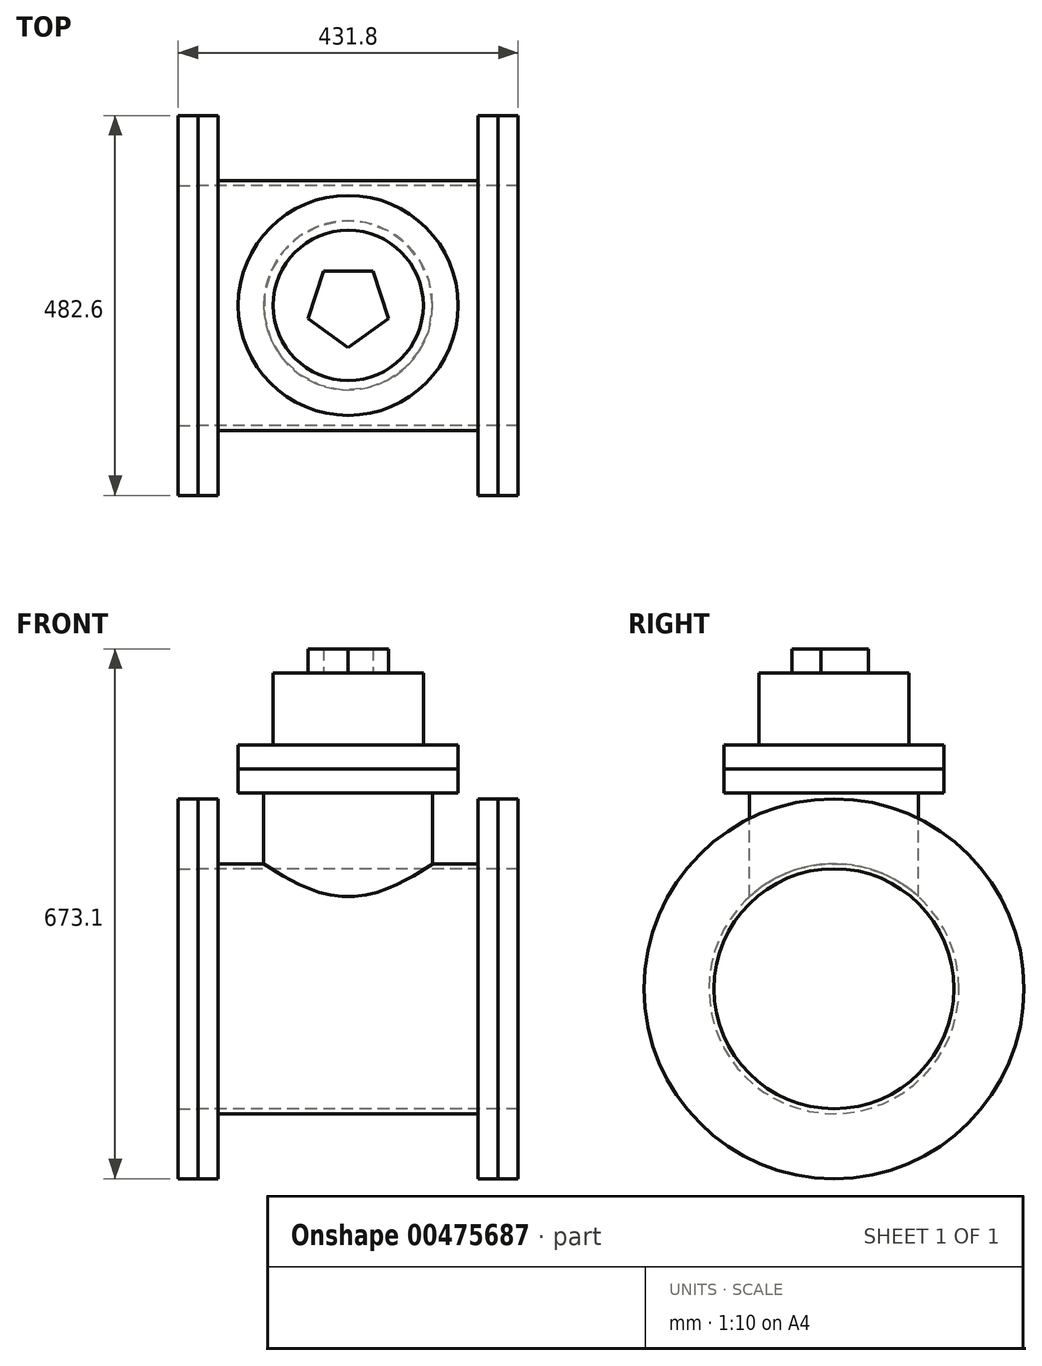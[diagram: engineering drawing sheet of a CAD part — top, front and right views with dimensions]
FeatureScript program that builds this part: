
annotation { "Feature Type Name" : "Feature", "Feature Type Description" : "" }
export const myFeature = defineFeature(function(context is Context, id is Id, definition is map)
    precondition{}
    {
        {
            var Q0;
            Q0=qCreatedBy(makeId("Right.planeOp"),FACE);
            var sketch = newSketch(context, id + "F0", { "sketchPlane" : qUnion([Q0])});
            skCircle(sketch, "E0", {"center": v(0, 0) * mm, "radius": 241.3 * mm});
            skCircle(sketch, "E1", {"center": v(0, 0) * mm, "radius": 152.4 * mm});
            skSolve(sketch);
        }
        {
            var Q0;
            Q0=makeQuery(id+"F0.imprint","IMPRINT",FACE,{"disambiguationData":[TD([[makeQuery(id+"F0.imprint","IMPRINT",EDGE,{"derivedFrom":sQuery(id+"F0.wireOp",EDGE,"E0")}),1.0]])]});
            extrude(context, id + "F1", {"entities" : qUnion([Q0]), "depth" : 25.4 * mm});
        }
        {
            var Q0;
            Q0=qCreatedBy(makeId("Right.planeOp"),FACE);
            cPlane(context, id + "F2", {"entities" : qUnion([Q0]), "cplaneType" : CPlaneType.OFFSET, "offset" : 330.2 * mm, "oppositeDirection" : true, "width" : 152.4 * mm, "height" : 152.4 * mm});
        }
        {
            var Q0;
            Q0=qCreatedBy(id+"F2.planeOp",FACE);
            var sketch = newSketch(context, id + "F3", { "sketchPlane" : qUnion([Q0])});
            skCircle(sketch, "E2", {"center": v(0, 0) * mm, "radius": 241.3 * mm});
            skCircle(sketch, "E3", {"center": v(0, 0) * mm, "radius": 152.4 * mm});
            skSolve(sketch);
        }
        {
            var Q0;
            Q0=makeQuery(id+"F3.imprint","IMPRINT",FACE,{"disambiguationData":[TD([[makeQuery(id+"F3.imprint","IMPRINT",EDGE,{"derivedFrom":sQuery(id+"F3.wireOp",EDGE,"E2")}),1.0]])]});
            extrude(context, id + "F4", {"entities" : qUnion([Q0]), "oppositeDirection" : true, "depth" : 25.4 * mm});
        }
        {
            var Q0;
            Q0=makeQuery(id+"F4.opExtrude","CAP_FACE",FACE,{"disambiguationData":[OSD([sQuery(id+"F3.wireOp",EDGE,"E2"),sQuery(id+"F3.wireOp",EDGE,"E3")])],"isStart":true});
            var sketch = newSketch(context, id + "F5", { "sketchPlane" : qUnion([Q0])});
            skPoint(sketch, "E4", {"position": v(0, 152.4) * mm});
            skSolve(sketch);
        }
        {
            var Q0;
            Q0=makeQuery(id+"F4.opExtrude","CAP_FACE",FACE,{"disambiguationData":[OSD([sQuery(id+"F3.wireOp",EDGE,"E2"),sQuery(id+"F3.wireOp",EDGE,"E3")])],"isStart":false});
            extrude(context, id + "F6", {"entities" : qUnion([Q0]), "depth" : 25.4 * mm});
        }
        {
            var Q0;
            Q0=makeQuery(id+"F1.opExtrude","CAP_FACE",FACE,{"disambiguationData":[OSD([sQuery(id+"F0.wireOp",EDGE,"E0"),sQuery(id+"F0.wireOp",EDGE,"E1")])],"isStart":false});
            extrude(context, id + "F7", {"entities" : qUnion([Q0]), "depth" : 25.4 * mm});
        }
        {
            var Q0;
            Q0=qCreatedBy(makeId("Top.planeOp"),FACE);
            var sketch = newSketch(context, id + "F8", { "sketchPlane" : qUnion([Q0])});
            skLineSegment(sketch, "E5", {"start": v(50.8, 0) * mm, "end": v(-381, 0) * mm, "construction": true});
            skPoint(sketch, "E6", {"position": v(-165.1, 0) * mm});
            skSolve(sketch);
        }
        {
            var Q0;
            Q0=makeQuery(id+"F5.imprint","IMPRINT",FACE,{"disambiguationData":[TD([[makeQuery(id+"F5.imprint","IMPRINT",EDGE,{"derivedFrom":makeQuery(id+"F4.opExtrude","CAP_EDGE",EDGE,{"disambiguationData":[OSD([sQuery(id+"F3.wireOp",EDGE,"E2")])],"isStart":true})}),1.0]])]});
            var sketch = newSketch(context, id + "F9", { "sketchPlane" : qUnion([Q0])});
            skCircle(sketch, "E7.0", {"center": v(0, 0) * mm, "radius": 152.4 * mm});
            skCircle(sketch, "E8", {"center": v(0, 0) * mm, "radius": 158.75 * mm});
            skSolve(sketch);
        }
        {
            var Q0;
            Q0=makeQuery(id+"F9.imprint","IMPRINT",FACE,{"disambiguationData":[TD([[makeQuery(id+"F9.imprint","IMPRINT",EDGE,{"derivedFrom":sQuery(id+"F9.wireOp",EDGE,"E7.0")}),-1.0]])]});
            var Q1;
            Q1=makeQuery(id+"F1.opExtrude","CAP_FACE",FACE,{"disambiguationData":[OSD([sQuery(id+"F0.wireOp",EDGE,"E0"),sQuery(id+"F0.wireOp",EDGE,"E1")])],"isStart":true});
            extrude(context, id + "F10", {"entities" : qUnion([Q0]), "operationType" : NewBodyOperationType.ADD, "endBound" : BoundingType.UP_TO_SURFACE, "endBoundEntityFace" : qUnion([Q1]), "depth" : 30.48 * mm});
        }
        {
            var Q0;
            Q0=qCreatedBy(makeId("Top.planeOp"),FACE);
            cPlane(context, id + "F11", {"entities" : qUnion([Q0]), "cplaneType" : CPlaneType.OFFSET, "offset" : 279.4 * mm, "width" : 152.4 * mm, "height" : 152.4 * mm});
        }
        {
            var Q0;
            Q0=qCreatedBy(id+"F11.planeOp",FACE);
            var sketch = newSketch(context, id + "F12", { "sketchPlane" : qUnion([Q0])});
            skCircle(sketch, "E9", {"center": v(-165.1, 0) * mm, "radius": 139.7 * mm});
            skSolve(sketch);
        }
        {
            var Q0;
            Q0=makeQuery(id+"F12.imprint","IMPRINT",FACE,{"disambiguationData":[TD([[makeQuery(id+"F12.imprint","IMPRINT",EDGE,{"derivedFrom":sQuery(id+"F12.wireOp",EDGE,"E9")}),1.0]])]});
            extrude(context, id + "F13", {"entities" : qUnion([Q0]), "oppositeDirection" : true, "depth" : 30.48 * mm});
        }
        {
            var Q0;
            Q0=makeQuery(id+"F13.opExtrude","CAP_FACE",FACE,{"disambiguationData":[OSD([sQuery(id+"F12.wireOp",EDGE,"E9")])],"isStart":false});
            var sketch = newSketch(context, id + "F14", { "sketchPlane" : qUnion([Q0])});
            skCircle(sketch, "E10", {"center": v(-165.1, 0) * mm, "radius": 107.36 * mm});
            skSolve(sketch);
        }
        {
            var Q0;
            Q0=makeQuery(id+"F14.imprint","IMPRINT",FACE,{"disambiguationData":[TD([[makeQuery(id+"F14.imprint","IMPRINT",EDGE,{"derivedFrom":sQuery(id+"F14.wireOp",EDGE,"E10")}),1.0]])]});
            var Q1;
            Q1=makeQuery(id+"F10.opExtrude","SWEPT_FACE",FACE,{"disambiguationData":[OSD([sQuery(id+"F9.wireOp",EDGE,"E8")])]});
            extrude(context, id + "F15", {"entities" : qUnion([Q0]), "operationType" : NewBodyOperationType.ADD, "endBound" : BoundingType.UP_TO_SURFACE, "endBoundEntityFace" : qUnion([Q1]), "depth" : 30.48 * mm});
        }
        {
            var Q0;
            Q0=makeQuery(id+"F13.opExtrude","CAP_FACE",FACE,{"disambiguationData":[OSD([sQuery(id+"F12.wireOp",EDGE,"E9")])],"isStart":true});
            extrude(context, id + "F16", {"entities" : qUnion([Q0]), "depth" : 30.48 * mm});
        }
        {
            var Q0;
            Q0=makeQuery(id+"F16.opExtrude","CAP_FACE",FACE,{"disambiguationData":[OSD([sQuery(id+"F12.wireOp",EDGE,"E9")])],"isStart":false});
            var sketch = newSketch(context, id + "F17", { "sketchPlane" : qUnion([Q0])});
            skCircle(sketch, "E11", {"center": v(-165.1, 0) * mm, "radius": 95.42 * mm});
            skSolve(sketch);
        }
        {
            var Q0;
            Q0=makeQuery(id+"F17.imprint","IMPRINT",FACE,{"disambiguationData":[TD([[makeQuery(id+"F17.imprint","IMPRINT",EDGE,{"derivedFrom":sQuery(id+"F17.wireOp",EDGE,"E11")}),1.0]])]});
            extrude(context, id + "F18", {"entities" : qUnion([Q0]), "operationType" : NewBodyOperationType.ADD, "depth" : 91.44 * mm});
        }
        {
            var Q0;
            Q0=makeQuery(id+"F18.opExtrude","CAP_FACE",FACE,{"disambiguationData":[OSD([sQuery(id+"F17.wireOp",EDGE,"E11")])],"isStart":false});
            var sketch = newSketch(context, id + "F19", { "sketchPlane" : qUnion([Q0])});
            skCircle(sketch, "E12.cCircle", {"center": v(-165.1, 0) * mm, "radius": 43.4 * mm, "construction": true});
            skLineSegment(sketch, "E12.0", {"start": v(-196.63, 43.4) * mm, "end": v(-133.57, 43.4) * mm});
            skLineSegment(sketch, "E12.1", {"start": v(-133.57, 43.4) * mm, "end": v(-114.08, -16.58) * mm});
            skLineSegment(sketch, "E12.2", {"start": v(-114.08, -16.58) * mm, "end": v(-165.1, -53.65) * mm});
            skLineSegment(sketch, "E12.3", {"start": v(-165.1, -53.65) * mm, "end": v(-216.12, -16.58) * mm});
            skLineSegment(sketch, "E12.4", {"start": v(-216.12, -16.58) * mm, "end": v(-196.63, 43.4) * mm});
            skPoint(sketch, "E12.0.midPoint", {"position": v(-165.1, 43.4) * mm});
            skSolve(sketch);
        }
        {
            var Q0;
            Q0=makeQuery(id+"F19.imprint","IMPRINT",FACE,{"disambiguationData":[TD([[makeQuery(id+"F19.imprint","IMPRINT",EDGE,{"derivedFrom":sQuery(id+"F19.wireOp",EDGE,"E12.0")}),-1.0]])]});
            extrude(context, id + "F20", {"entities" : qUnion([Q0]), "operationType" : NewBodyOperationType.ADD, "depth" : 30.48 * mm});
        }
    });
